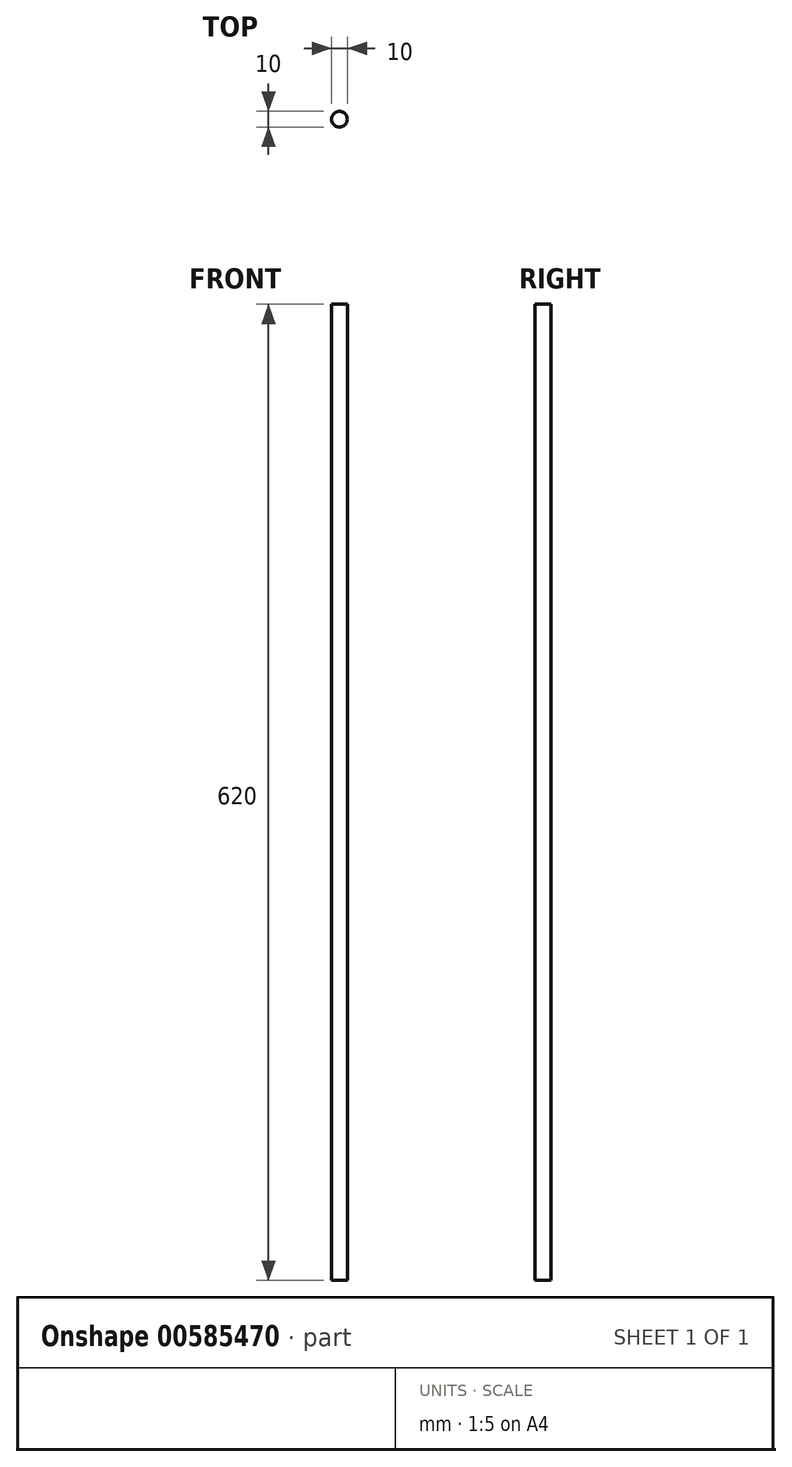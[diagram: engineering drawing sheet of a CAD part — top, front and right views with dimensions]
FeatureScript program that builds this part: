
annotation { "Feature Type Name" : "Feature", "Feature Type Description" : "" }
export const myFeature = defineFeature(function(context is Context, id is Id, definition is map)
    precondition{}
    {
        {
            var Q0;
            Q0=qCreatedBy(makeId("Top.planeOp"),FACE);
            var sketch = newSketch(context, id + "F0", { "sketchPlane" : qUnion([Q0])});
            skCircle(sketch, "E0", {"center": v(0, 0) * mm, "radius": 5 * mm});
            skSolve(sketch);
        }
        {
            var Q0;
            Q0 = qSketchRegion(id + "F0", true);
            extrude(context, id + "F1", {"entities" : qUnion([Q0]), "depth" : 620 * mm, "offsetDistance" : 25 * mm});
        }
    });
